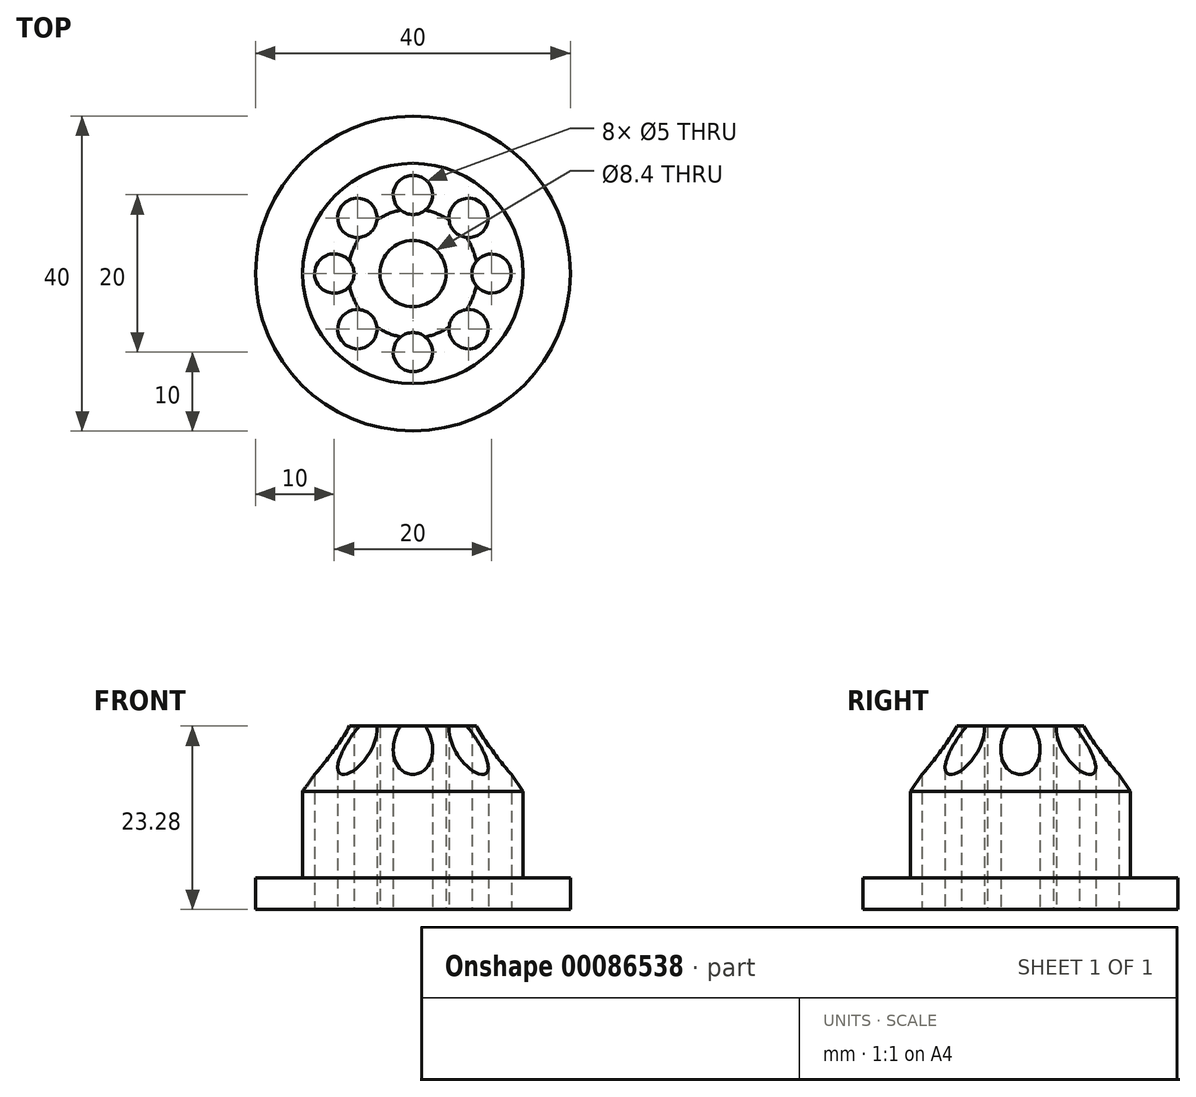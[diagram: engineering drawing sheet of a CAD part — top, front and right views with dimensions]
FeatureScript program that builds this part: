
annotation { "Feature Type Name" : "Feature", "Feature Type Description" : "" }
export const myFeature = defineFeature(function(context is Context, id is Id, definition is map)
    precondition{}
    {
        {
            var Q0;
            Q0=qCreatedBy(makeId("Front.planeOp"),FACE);
            var sketch = newSketch(context, id + "F0", { "sketchPlane" : qUnion([Q0])});
            skLineSegment(sketch, "E0", {"start": v(0, 0) * mm, "end": v(0, 62.9) * mm, "construction": true});
            skLineSegment(sketch, "E1", {"start": v(-4.2, 0) * mm, "end": v(-20, 0) * mm});
            skLineSegment(sketch, "E2", {"start": v(-20, 0) * mm, "end": v(-20, 4) * mm});
            skLineSegment(sketch, "E3", {"start": v(-20, 4) * mm, "end": v(-14, 4) * mm});
            skLineSegment(sketch, "E4", {"start": v(-14, 4) * mm, "end": v(-14, 15) * mm});
            skLineSegment(sketch, "E5", {"start": v(-14, 15) * mm, "end": v(-8.2, 23.28) * mm});
            skLineSegment(sketch, "E6", {"start": v(-8.2, 23.28) * mm, "end": v(-4.2, 23.28) * mm});
            skLineSegment(sketch, "E7", {"start": v(-4.2, 23.28) * mm, "end": v(-4.2, 0) * mm});
            skSolve(sketch);
        }
        {
            var Q0;
            Q0=makeQuery(id+"F0.imprint","IMPRINT",FACE,{"disambiguationData":[TD([[makeQuery(id+"F0.imprint","IMPRINT",EDGE,{"derivedFrom":sQuery(id+"F0.wireOp",EDGE,"E1")}),-1.0]])]});
            var Q1;
            Q1=sQuery(id+"F0.wireOp",EDGE,"E0");
            revolve(context, id + "F1", {"entities" : qUnion([Q0]), "axis" : qUnion([Q1]), "revolveType" : RevolveType.FULL});
        }
        {
            var Q0;
            Q0=qCreatedBy(makeId("Top.planeOp"),FACE);
            var sketch = newSketch(context, id + "F2", { "sketchPlane" : qUnion([Q0])});
            skCircle(sketch, "E8", {"center": v(0, 0) * mm, "radius": 10 * mm, "construction": true});
            skCircle(sketch, "E9", {"center": v(0, -10) * mm, "radius": 2.5 * mm});
            skCircle(sketch, "E10.1.0", {"center": v(7.07, -7.07) * mm, "radius": 2.5 * mm});
            skCircle(sketch, "E10.2.0", {"center": v(10, 0) * mm, "radius": 2.5 * mm});
            skCircle(sketch, "E10.3.0", {"center": v(7.07, 7.07) * mm, "radius": 2.5 * mm});
            skCircle(sketch, "E10.4.0", {"center": v(0, 10) * mm, "radius": 2.5 * mm});
            skCircle(sketch, "E10.5.0", {"center": v(-7.07, 7.07) * mm, "radius": 2.5 * mm});
            skCircle(sketch, "E10.6.0", {"center": v(-10, 0) * mm, "radius": 2.5 * mm});
            skCircle(sketch, "E10.7.0", {"center": v(-7.07, -7.07) * mm, "radius": 2.5 * mm});
            skSolve(sketch);
        }
        {
            var Q0;
            Q0 = qSketchRegion(id + "F2", true);
            extrude(context, id + "F3", {"entities" : qUnion([Q0]), "operationType" : NewBodyOperationType.REMOVE, "depth" : 25 * mm});
        }
    });
